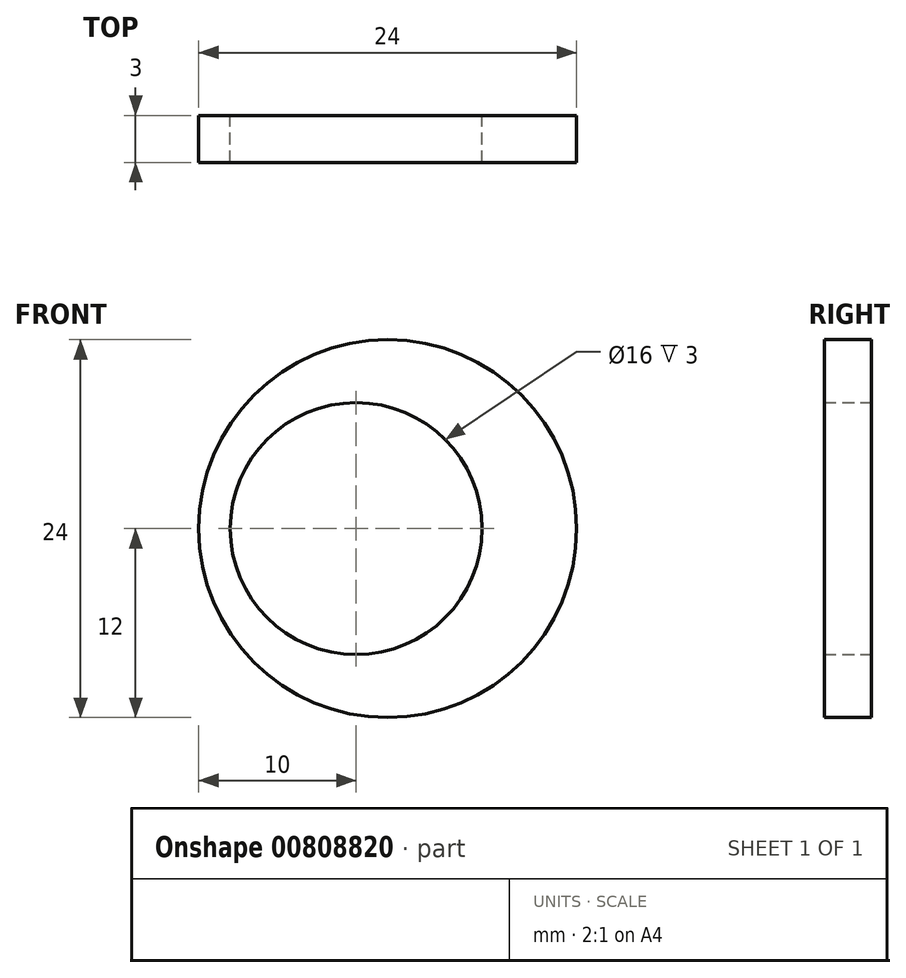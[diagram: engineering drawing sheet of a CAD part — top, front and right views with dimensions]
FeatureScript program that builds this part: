
annotation { "Feature Type Name" : "Feature", "Feature Type Description" : "" }
export const myFeature = defineFeature(function(context is Context, id is Id, definition is map)
    precondition{}
    {
        {
            var Q0;
            Q0=qCreatedBy(makeId("Front.planeOp"),FACE);
            var sketch = newSketch(context, id + "F0", { "sketchPlane" : qUnion([Q0])});
            skCircle(sketch, "E0", {"center": v(0, 0) * mm, "radius": 12 * mm});
            skCircle(sketch, "E1", {"center": v(-2, 0) * mm, "radius": 8 * mm});
            skSolve(sketch);
        }
        {
            var Q0;
            Q0=qSketchRegion(id+"F0",true);
            extrude(context, id + "F1", {"entities" : qUnion([Q0]), "depth" : 3 * mm, "offsetDistance" : 25 * mm});
        }
    });
